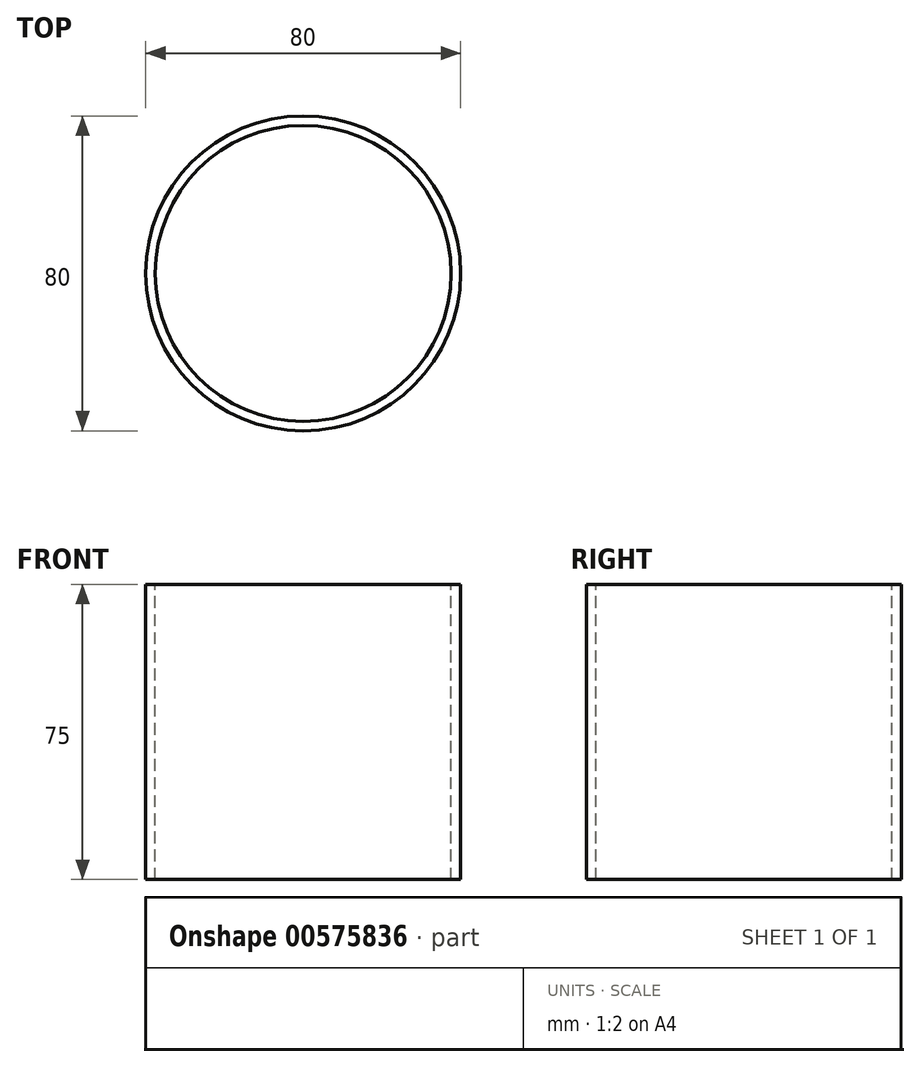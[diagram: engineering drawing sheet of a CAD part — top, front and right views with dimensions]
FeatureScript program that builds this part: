
annotation { "Feature Type Name" : "Feature", "Feature Type Description" : "" }
export const myFeature = defineFeature(function(context is Context, id is Id, definition is map)
    precondition{}
    {
        {
            var Q0;
            Q0=qCreatedBy(makeId("Top.planeOp"),FACE);
            var sketch = newSketch(context, id + "F0", { "sketchPlane" : qUnion([Q0])});
            skCircle(sketch, "E0", {"center": v(0, 0) * mm, "radius": 40 * mm});
            skSolve(sketch);
        }
        {
            var Q0;
            Q0=makeQuery(id+"F0.imprint","IMPRINT",FACE,{"disambiguationData":[TD([[makeQuery(id+"F0.imprint","IMPRINT",EDGE,{"derivedFrom":sQuery(id+"F0.wireOp",EDGE,"E0")}),1.0]])]});
            var sketch = newSketch(context, id + "F1", { "sketchPlane" : qUnion([Q0])});
            skCircle(sketch, "E1", {"center": v(0, 0) * mm, "radius": 37.58 * mm});
            skSolve(sketch);
        }
        {
            var Q0;
            Q0=sQuery(id+"F0.wireOp",EDGE,"E0");
            var Q1;
            Q1=sQuery(id+"F1.wireOp",EDGE,"E1");
            extrude(context, id + "F2", {"bodyType" : ToolBodyType.SURFACE, "surfaceEntities" : qUnion([Q0, Q1]), "depth" : 75 * mm, "offsetDistance" : 25 * mm});
        }
    });
